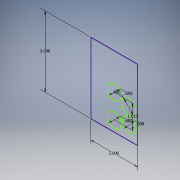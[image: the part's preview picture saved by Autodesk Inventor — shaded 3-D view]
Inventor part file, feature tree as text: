
AUTODESK INVENTOR PART (.ipt)
format: ipt  version: 2017 (Build 210142000, 142)  size: 93,184 bytes
history: native  units: in
note: dims shown in document units (in); Inventor stores cm internally (conversion verified against a paired STEP export)
features: sketch x1
ambient origin geometry x8: Origin, YZ Plane, XZ Plane, XY Plane, X Axis, Y Axis, Z Axis, Center Point
feature tree (1):
  sketch  "Sketch1"  dims[d0=2.0in d1=3.0in d2=0.6in d3=0.6in d4=0.6in d5=0.6in d6=1.0125in]
